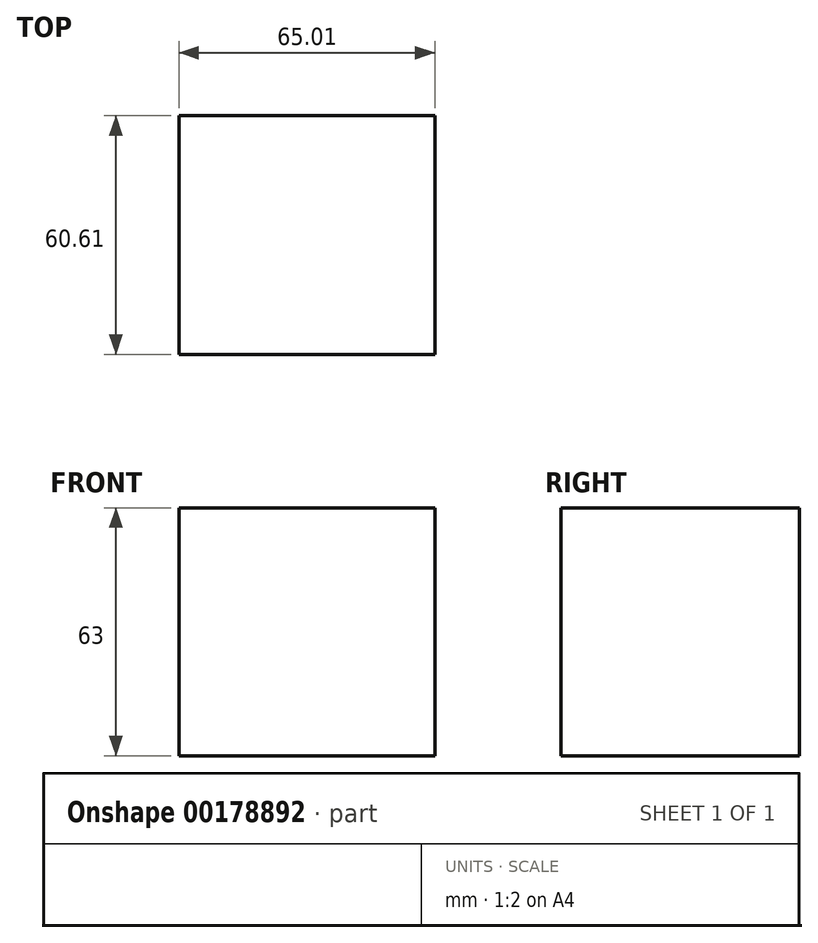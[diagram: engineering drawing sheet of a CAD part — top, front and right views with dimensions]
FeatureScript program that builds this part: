
annotation { "Feature Type Name" : "Feature", "Feature Type Description" : "" }
export const myFeature = defineFeature(function(context is Context, id is Id, definition is map)
    precondition{}
    {
        {
            var Q0;
            Q0=qCreatedBy(makeId("Top.planeOp"),FACE);
            var sketch = newSketch(context, id + "F0", { "sketchPlane" : qUnion([Q0])});
            skLineSegment(sketch, "E0.bottom", {"start": v(0, 0) * mm, "end": v(65, 0) * mm});
            skLineSegment(sketch, "E0.top", {"start": v(0, -60.6) * mm, "end": v(65, -60.6) * mm});
            skLineSegment(sketch, "E0.left", {"start": v(0, 0) * mm, "end": v(0, -60.6) * mm});
            skLineSegment(sketch, "E0.right", {"start": v(65, 0) * mm, "end": v(65, -60.6) * mm});
            skSolve(sketch);
        }
        {
            var Q0;
            Q0 = qSketchRegion(id + "F0", true);
            extrude(context, id + "F1", {"entities" : qUnion([Q0]), "depth" : 63 * mm});
        }
    });
